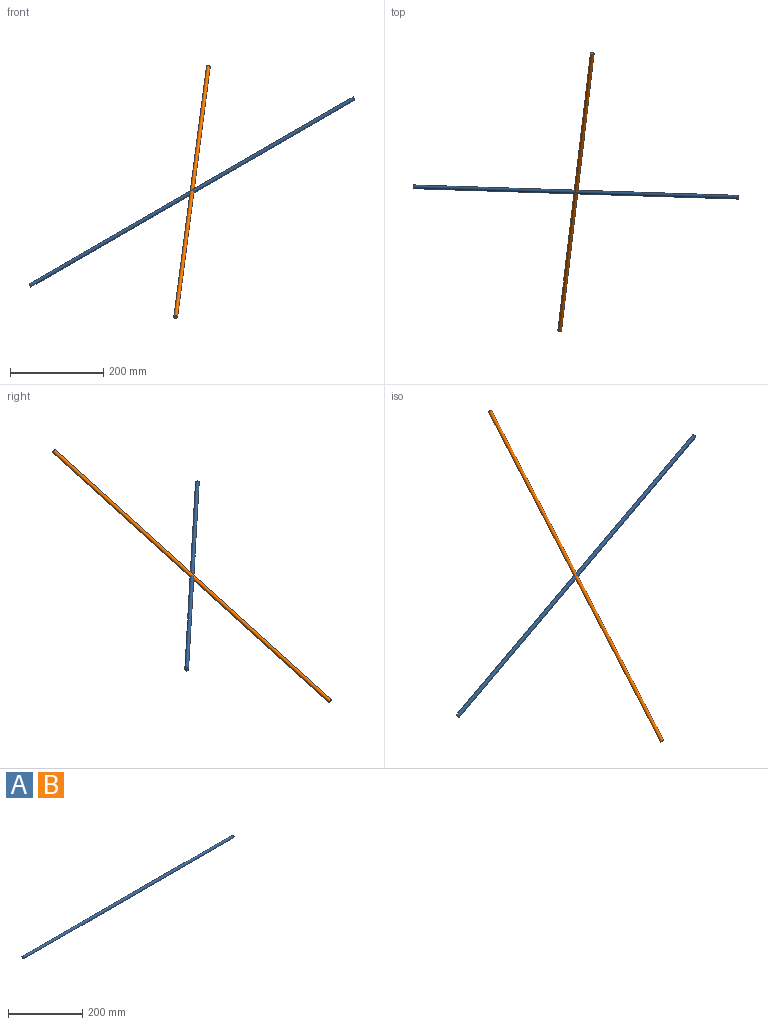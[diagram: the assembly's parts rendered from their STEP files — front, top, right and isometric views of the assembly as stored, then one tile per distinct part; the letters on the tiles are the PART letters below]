
ASSEMBLY  parts=2 mates=1
PART A: 3 faces, bbox 801x8x8 mm
  f0: plane 8x8mm, normal (-1,0,0), area 50.3mm2, adj f2
  f1: plane 8x8mm, normal (1,0,0), area 50.3mm2, adj f2
  f2: cylinder r=4mm len=801mm, axis (1,0,0), area 20131.3mm2, adj f0,f1
PART B: same geometry as A
PLACE A rot(axis=(0.88,-0.42,0.21),67.3deg) t=(-126.21,658.41,315.52)mm
PLACE B rot(axis=(0.31,0.34,-0.89),101.8deg) t=(-130.2,655.44,310.63)mm
MATE ball A.f2 <-> B.f2  axis (0.87,-0.03,0.5) through (-130.71,627.24,333.16)mm
